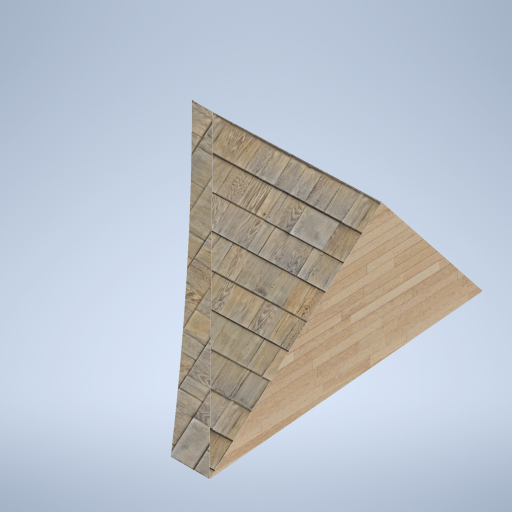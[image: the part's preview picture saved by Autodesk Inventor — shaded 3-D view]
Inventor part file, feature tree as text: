
AUTODESK INVENTOR PART (.ipt)
format: ipt  version: 2024.2 (Build 282272000, 272)  size: 472,064 bytes
history: native  units: mm
features: sketch x7, plane x5, loft x2, extrude x2, projected_geometry x2, other x1
ambient origin geometry x8: Origin, YZ Plane, XZ Plane, XY Plane, X Axis, Y Axis, Z Axis, Center Point
bodies: Solid1 (feature_tree)
feature tree (19):
  sketch  "Sketch1"  dims[d5=0.0mm d6=-8101.0mm d7=800.0mm]
  plane  "Work Plane2"
  loft  "Loft1"
  plane  "Work Plane3"
  extrude  "Extrusion1"  TaperAngle=0.0deg  [1 undecoded]
  sketch  "Sketch5"  dims[d15=6.981317mm d16=0.0mm d17=0.0mm]
  plane  "Work Plane4"
  extrude  "Extrusion2"  TaperAngle=0.0deg  [1 undecoded]
  plane  "Work Plane5"
  sketch  "Sketch7"  dims[d19=0.0mm d20=90.0deg]
  sketch  "Sketch8"  dims[d21=0.0mm d22=90.0deg]
  loft  "Loft2"
  plane  "Work Plane1"
  sketch  "Sketch2"  dims[d8=0.0mm d9=90.0deg d10=0.0mm d11=90.0deg]
  sketch  "Sketch3"  dims[d12=2600.0mm d13=0.0mm d14=0.0mm]
  sketch  "Sketch6"  dims[d18=90.0deg]
  projected_geometry  "Projected Loop1"
  projected_geometry  "Projected Loop2"
  other  "Edges1"
note: 2 required parameter values undecoded (feature->parameter linkage not recoverable at this tier; creation-order binding heuristic only, values carry confidence <= 0.55)
